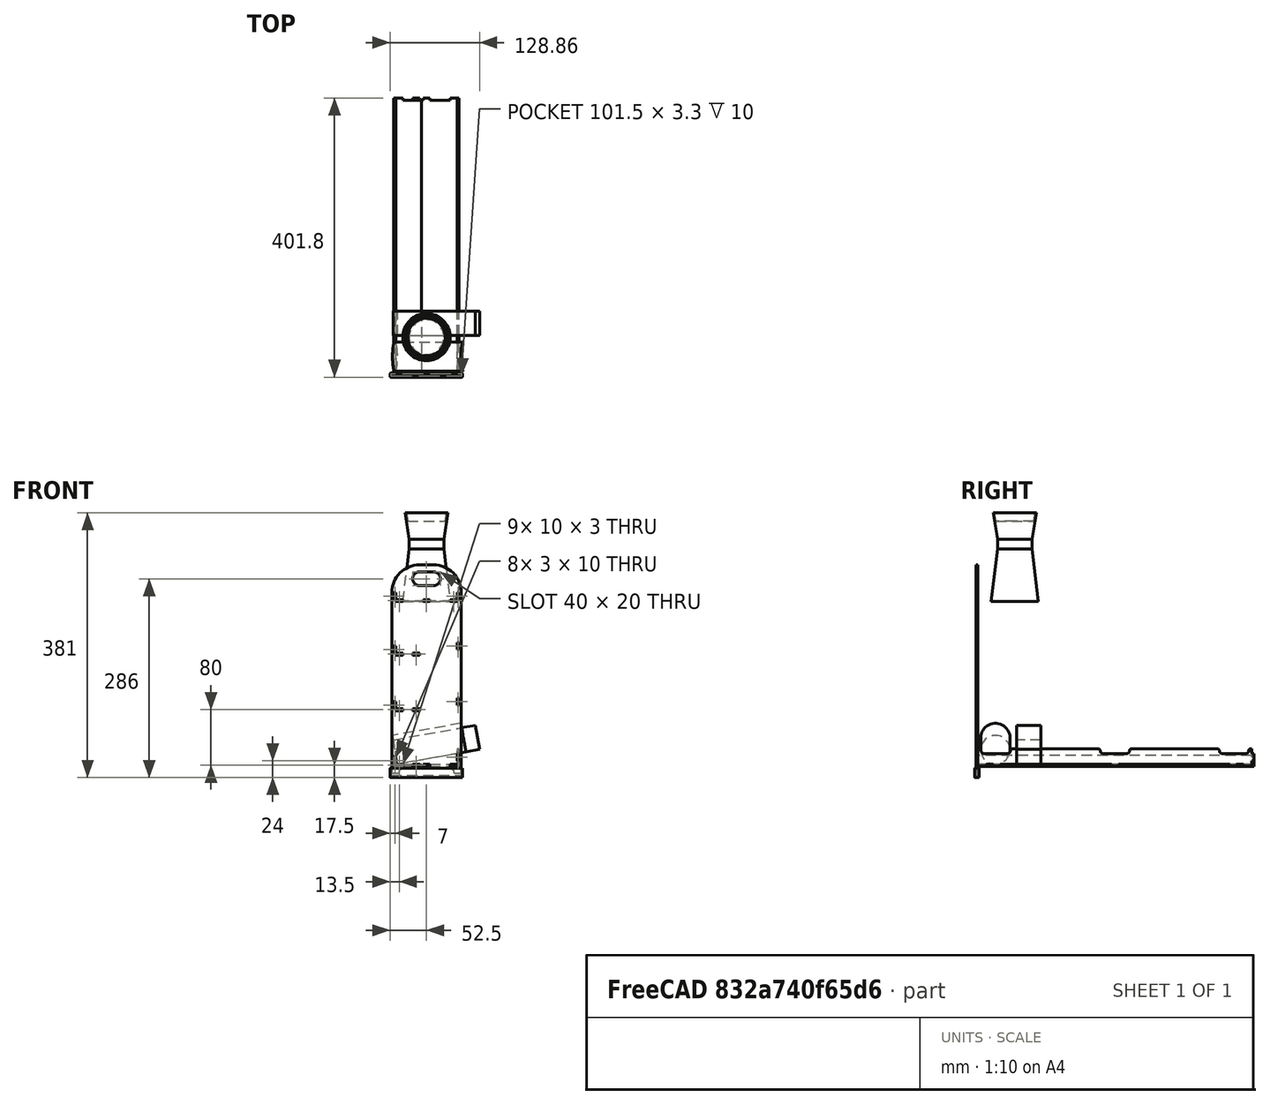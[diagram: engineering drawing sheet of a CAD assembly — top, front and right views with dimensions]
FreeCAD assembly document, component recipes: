
FREECAD ASSEMBLY — COMPONENT RECIPES ("stockage_epices")

This assembly document has 12 components, labeled P0..P11 below (a component is one placed body or linked part). 12 of them carry a construction recipe — the FreeCAD feature program that regenerates the part from scratch, quoted from this document or its linked companion documents; the rest are supplied as boundary geometry only. No exploded tour is included for this assembly.
COMPONENT P0 — recipe-attached ("BackR003", modeled in this document).
Construction recipe (the document's own serialized feature program — sketch geometry with constraints, then the solid features built on it; lengths are millimeters unless a unit is written):

FEATURE [Sketcher::SketchObject] Sketch004
  ArcFitTolerance = 0
  FullyConstrained = true
  MakeInternals = false
  MapMode = 5
  Placement = pos=(0,0,0) rot=(0.57735,0.57735,0.57735;2.0944rad)
  sketch-geometry (12):
    g0: LineSegment StartX=394 StartY=0 StartZ=0 EndX=0 EndY=0 EndZ=0
    g1: LineSegment StartX=394 StartY=-13 StartZ=0 EndX=397 EndY=-13 EndZ=0
    g2: LineSegment StartX=397 StartY=-13 StartZ=0 EndX=397 EndY=-3 EndZ=0
    g3: LineSegment StartX=397 StartY=-3 StartZ=0 EndX=394 EndY=-3 EndZ=0
    g4: LineSegment StartX=0 StartY=-3 StartZ=0 EndX=-3 EndY=-3 EndZ=0
    g5: LineSegment StartX=-3 StartY=-3 StartZ=0 EndX=-3 EndY=-13 EndZ=0
    g6: LineSegment StartX=-3 StartY=-13 StartZ=0 EndX=0 EndY=-13 EndZ=0
    g7: LineSegment StartX=0 StartY=-3 StartZ=0 EndX=0 EndY=0 EndZ=0
    g8: LineSegment StartX=0 StartY=-13 StartZ=0 EndX=0 EndY=-16 EndZ=0
    g9: LineSegment StartX=394 StartY=-3 StartZ=0 EndX=394 EndY=0 EndZ=0
    g10: LineSegment StartX=394 StartY=-13 StartZ=0 EndX=394 EndY=-16 EndZ=0
    g11: LineSegment StartX=0 StartY=-16 StartZ=0 EndX=394 EndY=-16 EndZ=0
  constraints (36):
    c: Horizontal(g0)
    c: Distance(g0,g0) = 394
    c: Coincident(g1,g2)
    c: Coincident(g2,g3)
    c: Horizontal(g1)
    c: Horizontal(g3)
    c: Vertical(g2)
    c: Distance(g2,g1) = 3
    c: Coincident(g4,g5)
    c: Coincident(g5,g6)
    c: Horizontal(g4)
    c: Horizontal(g6)
    c: Vertical(g5)
    c: Distance(g5,g4) = 3
    c: Equal(g5,g2)
    c: Horizontal(g1,g5)
    c: DistanceY(g5,g5) = 10
    c: DistanceY(g4,g0) = 3
    c: Coincident(g7,g4)
    c: Coincident(g7,g0)
    c: Vertical(g7)
    c: Coincident(g8,g6)
    c: PointOnObject(g8,g-2)
    c: Vertical(g8)
    c: Coincident(g9,g3)
    c: Coincident(g9,g0)
    c: Vertical(g9)
    c: Coincident(g10,g1)
    c: Vertical(g10)
    c: Equal(g1,g3)
    c: PointOnObject(g0,g-1)
    c: PointOnObject(g4,g-2)
    c: Equal(g7,g8)
    c: Equal(g9,g10)
    c: Coincident(g11,g8)
    c: Coincident(g11,g10)
FEATURE [PartDesign::Pad] Pad003
  Direction = (1,1e-16,-1e-16)
  Length = 3
  Length2 = 10
  Placement = pos=(0,0,0) rot=(0.57735,0.57735,0.57735;2.0944rad)
  Profile = -> Sketch004
  Refine = true
  Suppressed = false
  Type = 0
FEATURE [Sketcher::SketchObject] Sketch005
  ArcFitTolerance = 0
  ExternalGeometry = -> [Pad003]
  FullyConstrained = true
  MakeInternals = false
  MapMode = 5
  Placement = pos=(3,-1e-15,0) rot=(0.57735,0.57735,0.57735;2.0944rad)
  sketch-geometry (4):
    g0: LineSegment StartX=12 StartY=-16 StartZ=0 EndX=22 EndY=-16 EndZ=0
    g1: LineSegment StartX=22 StartY=-16 StartZ=0 EndX=22 EndY=-13 EndZ=0
    g2: LineSegment StartX=22 StartY=-13 StartZ=0 EndX=12 EndY=-13 EndZ=0
    g3: LineSegment StartX=12 StartY=-13 StartZ=0 EndX=12 EndY=-16 EndZ=0
  constraints (12):
    c: Coincident(g0,g1)
    c: Coincident(g1,g2)
    c: Coincident(g2,g3)
    c: Coincident(g3,g0)
    c: Horizontal(g0)
    c: Horizontal(g2)
    c: Vertical(g1)
    c: Vertical(g3)
    c: Distance(g1,g3) = 10
    c: Distance(g0,g2) = 3
    c: PointOnObject(g0,g-3)
    c: DistanceX(g-1,g2) = 12
FEATURE [PartDesign::Pocket] Pocket001
  BaseFeature = -> Pad003
  Direction = (-1,-1e-16,1e-16)
  Length = 5
  Length2 = 5
  Placement = pos=(0,0,0) rot=(0.57735,0.57735,0.57735;2.0944rad)
  Profile = -> Sketch005
  Refine = true
  Suppressed = false
  Type = 2
FEATURE [PartDesign::LinearPattern] LinearPattern001
  BaseFeature = -> Pocket001
  Direction = -> Sketch005 [H_Axis]
  Length = 360
  Mode = 0
  Occurrences = 3
  Offset = 180
  Originals = -> [Pocket001]
  Placement = pos=(0,0,0) rot=(0.57735,0.57735,0.57735;2.0944rad)
  Refine = true
  Suppressed = false
  TransformMode = 0
FEATURE [PartDesign::Body] Body003  label="BackR1"
  AllowCompound = false
  Group = -> [Sketch004,Pad003,Sketch005,Pocket001,LinearPattern001]
  Origin = -> Origin003
  Placement = pos=(0,0,29) rot=(0,0,1;0rad)
  Tip = -> LinearPattern001
COMPONENT P1 — same part as P0; its construction recipe is shown at P0.
COMPONENT P2 — recipe-attached ("Epice_rond", modeled in this document).
Construction recipe (the document's own serialized feature program — sketch geometry with constraints, then the solid features built on it; lengths are millimeters unless a unit is written):

FEATURE [Sketcher::SketchObject] Sketch
  ArcFitTolerance = 0
  FullyConstrained = true
  MakeInternals = false
  MapMode = 5
  Placement = pos=(0,0,0) rot=(0.57735,0.57735,0.57735;2.0944rad)
  sketch-geometry (1):
    g0: Circle CenterX=0 CenterY=0 CenterZ=0 NormalX=0 NormalY=0 NormalZ=1 AngleXU=0 Radius=21
  constraints (2):
    c: Diameter(g0) = 42
    c: Coincident(g0,g-1)
FEATURE [PartDesign::Pad] Pad
  Direction = (1,1e-16,-1e-16)
  Length = 100
  Length2 = 10
  Placement = pos=(0,0,0) rot=(0.57735,0.57735,0.57735;2.0944rad)
  Profile = -> Sketch
  Refine = true
  Suppressed = false
  Type = 0
FEATURE [PartDesign::Body] Body  label="Epice_rond"
  AllowCompound = false
  Group = -> [Sketch,Pad]
  Origin = -> Origin
  Placement = pos=(1.62713,25,36.8423) rot=(0,-1,0;0.174533rad)
  Tip = -> Pad
COMPONENT P3 — recipe-attached ("Epice_carre", modeled in this document).
Construction recipe (the document's own serialized feature program — sketch geometry with constraints, then the solid features built on it; lengths are millimeters unless a unit is written):

FEATURE [Sketcher::SketchObject] Sketch001
  ArcFitTolerance = 0
  FullyConstrained = true
  MakeInternals = false
  MapMode = 5
  Placement = pos=(0,0,0) rot=(0.57735,0.57735,0.57735;2.0944rad)
  sketch-geometry (5):
    g0: LineSegment StartX=-17.5 StartY=-17.5 StartZ=0 EndX=17.5 EndY=-17.5 EndZ=0
    g1: LineSegment StartX=17.5 StartY=-17.5 StartZ=0 EndX=17.5 EndY=17.5 EndZ=0
    g2: LineSegment StartX=17.5 StartY=17.5 StartZ=0 EndX=-17.5 EndY=17.5 EndZ=0
    g3: LineSegment StartX=-17.5 StartY=17.5 StartZ=0 EndX=-17.5 EndY=-17.5 EndZ=0
    g4: GeomPoint [constr] X=0 Y=0 Z=0
  constraints (12):
    c: Coincident(g0,g1)
    c: Coincident(g1,g2)
    c: Coincident(g2,g3)
    c: Coincident(g3,g0)
    c: Horizontal(g0)
    c: Horizontal(g2)
    c: Vertical(g1)
    c: Vertical(g3)
    c: Symmetric(g2,g0,g4)
    c: Distance(g1,g3) = 35
    c: Distance(g0,g2) = 35
    c: Coincident(g4,g-1)
FEATURE [PartDesign::Pad] Pad001
  Direction = (1,1e-16,-1e-16)
  Length = 120
  Length2 = 10
  Placement = pos=(0,0,0) rot=(0.57735,0.57735,0.57735;2.0944rad)
  Profile = -> Sketch001
  Refine = true
  Suppressed = false
  Type = 0
FEATURE [PartDesign::Body] Body001  label="Epice_carre"
  AllowCompound = false
  Group = -> [Sketch001,Pad001]
  Origin = -> Origin001
  Placement = pos=(2.14807,73,33.8878) rot=(0,-1,0;0.174533rad)
  Tip = -> Pad001
COMPONENT P4 — recipe-attached ("GratGrat", modeled in this document).
Construction recipe (the document's own serialized feature program — sketch geometry with constraints, then the solid features built on it; lengths are millimeters unless a unit is written):

FEATURE [Sketcher::SketchObject] Sketch013
  ArcFitTolerance = 0
  FullyConstrained = true
  MakeInternals = false
  MapMode = 5
  Placement = pos=(0,0,0) rot=(1,0,0;1.5708rad)
  sketch-geometry (8):
    g0: LineSegment StartX=0 StartY=0 StartZ=0 EndX=-34 EndY=0 EndZ=0
    g1: LineSegment StartX=-34 StartY=0 StartZ=0 EndX=-25 EndY=76 EndZ=0
    g2: LineSegment StartX=-25 StartY=76 StartZ=0 EndX=-25 EndY=90 EndZ=0
    g3: LineSegment StartX=-25 StartY=90 StartZ=0 EndX=-31 EndY=128 EndZ=0
    g4: LineSegment StartX=-31 StartY=128 StartZ=0 EndX=-29 EndY=128 EndZ=0
    g5: LineSegment StartX=-29 StartY=128 StartZ=0 EndX=-27.1053 EndY=116 EndZ=0
    g6: LineSegment StartX=-27.1053 StartY=116 StartZ=0 EndX=0 EndY=116 EndZ=0
    g7: LineSegment StartX=0 StartY=116 StartZ=0 EndX=0 EndY=0 EndZ=0
  constraints (23):
    c: Coincident(g-1,g0)
    c: Horizontal(g0)
    c: Coincident(g0,g1)
    c: Coincident(g1,g2)
    c: Vertical(g2)
    c: Coincident(g2,g3)
    c: Coincident(g3,g4)
    c: Horizontal(g4)
    c: Coincident(g4,g5)
    c: Coincident(g5,g6)
    c: Horizontal(g6)
    c: Coincident(g6,g7)
    c: Coincident(g7,g0)
    c: Vertical(g7)
    c: DistanceX(g0,g0) = 34
    c: Distance(g7,g2) = 25
    c: Distance(g3,g-2) = 31
    c: Parallel(g5,g3)
    c: DistanceY(g2,g2) = 14
    c: DistanceY(g0,g1) = 76
    c: Distance(g4,g4) = 2
    c: DistanceY(g0,g3) = 128
    c: DistanceY(g6,g4) = 12
FEATURE [PartDesign::Revolution] Revolution
  Angle = 360
  Angle2 = 60
  Axis = (0,0,1)
  Base = (0,0,0)
  Placement = pos=(0,0,0) rot=(1,0,0;1.5708rad)
  Profile = -> Sketch013
  ReferenceAxis = -> Sketch013 [V_Axis]
  Refine = true
  Suppressed = false
  Type = 0
FEATURE [PartDesign::Body] Body007  label="GratGrat"
  AllowCompound = false
  Group = -> [Sketch013,Revolution]
  Origin = -> Origin010
  Placement = pos=(47,53,250) rot=(0,0,1;0rad)
  Tip = -> Revolution
COMPONENT P5 — recipe-attached ("Part001", modeled in this document).
Construction recipe (the document's own serialized feature program — sketch geometry with constraints, then the solid features built on it; lengths are millimeters unless a unit is written):

FEATURE [Sketcher::SketchObject] Sketch015
  ArcFitTolerance = 1e-06
  AttachmentSupport = -> [XY_Plane012]
  FullyConstrained = true
  MakeInternals = false
  MapMode = 5
  sketch-geometry (14):
    g0: LineSegment StartX=-4 StartY=0 StartZ=0 EndX=-4 EndY=-3.3 EndZ=0
    g1: LineSegment StartX=-4 StartY=-3.3 StartZ=0 EndX=97.5 EndY=-3.3 EndZ=0
    g2: LineSegment StartX=97.5 StartY=-3.3 StartZ=0 EndX=97.5 EndY=0 EndZ=0
    g3: LineSegment StartX=97.5 StartY=0 StartZ=0 EndX=-4 EndY=0 EndZ=0
    g4: LineSegment StartX=-5.5 StartY=2e-16 StartZ=0 EndX=-5.5 EndY=-3.3 EndZ=0
    g5: LineSegment StartX=-4 StartY=-4.8 StartZ=0 EndX=97.5 EndY=-4.8 EndZ=0
    g6: LineSegment StartX=99 StartY=-3.3 StartZ=0 EndX=99 EndY=0 EndZ=0
    g7: LineSegment StartX=97.5 StartY=1.5 StartZ=0 EndX=-4 EndY=1.5 EndZ=0
    g8: ArcOfCircle CenterX=-4 CenterY=0 CenterZ=0 NormalX=0 NormalY=0 NormalZ=1 AngleXU=0 Radius=1.5 StartAngle=1.5708 EndAngle=3.14159
    g9: ArcOfCircle CenterX=-4 CenterY=-3.3 CenterZ=0 NormalX=0 NormalY=0 NormalZ=1 AngleXU=0 Radius=1.5 StartAngle=3.14159 EndAngle=4.71239
    g10: ArcOfCircle CenterX=97.5 CenterY=-3.3 CenterZ=0 NormalX=0 NormalY=0 NormalZ=1 AngleXU=0 Radius=1.5 StartAngle=4.71239 EndAngle=6.28319
    g11: ArcOfCircle CenterX=97.5 CenterY=1e-16 CenterZ=0 NormalX=0 NormalY=0 NormalZ=1 AngleXU=0 Radius=1.5 StartAngle=0 EndAngle=1.5708
    g12: GeomPoint [constr] X=-5.5 Y=1.5 Z=0
    g13: GeomPoint [constr] X=99 Y=-4.8 Z=0
  constraints (34):
    c: Coincident(g0,g1)
    c: Coincident(g1,g2)
    c: Coincident(g2,g3)
    c: Coincident(g3,g0)
    c: Vertical(g0)
    c: Vertical(g2)
    c: Horizontal(g1)
    c: Horizontal(g3)
    c: Distance(g0,g2) = 101.5
    c: Distance(g1,g3) = 3.3
    c: PointOnObject(g0,g-1)
    c: Tangent(g4,g8) = -1.5708
    c: Tangent(g4,g9) = -1.5708
    c: Tangent(g5,g9) = -1.5708
    c: Tangent(g5,g10) = -1.5708
    c: Tangent(g6,g10) = -1.5708
    c: Tangent(g6,g11) = -1.5708
    c: Tangent(g7,g11) = -1.5708
    c: Tangent(g7,g8) = -1.5708
    c: Vertical(g4)
    c: Vertical(g6)
    c: Horizontal(g5)
    c: Horizontal(g7)
    c: Equal(g8,g9)
    c: Equal(g9,g10)
    c: Equal(g10,g11)
    c: PointOnObject(g12,g4)
    c: PointOnObject(g12,g7)
    c: PointOnObject(g13,g5)
    c: PointOnObject(g13,g6)
    c: Radius(g9) = 1.5
    c: Coincident(g8,g0)
    c: Coincident(g10,g1)
    c: Distance(g-2,g0) = 4
FEATURE [PartDesign::Pad] Pad007
  Direction = (0,0,1)
  Length = 10
  Length2 = 10
  Profile = -> Sketch015
  ReferenceAxis = -> Sketch015 [N_Axis]
  Suppressed = false
  Type = 0
FEATURE [Sketcher::SketchObject] Sketch016
  ArcFitTolerance = 1e-06
  AttachmentSupport = -> [Pad007]
  ExternalGeometry = -> [Pad007]
  FullyConstrained = true
  MakeInternals = false
  MapMode = 5
  Placement = pos=(0,0,0) rot=(1,0,0;3.14159rad)
  sketch-geometry (10):
    g0: LineSegment StartX=-5.5 StartY=3.3 StartZ=0 EndX=-5.5 EndY=0 EndZ=0
    g1: LineSegment StartX=-4 StartY=-1.5 StartZ=0 EndX=97.5 EndY=-1.5 EndZ=0
    g2: LineSegment StartX=99 StartY=-1e-16 StartZ=0 EndX=99 EndY=3.3 EndZ=0
    g3: LineSegment StartX=97.5 StartY=4.8 StartZ=0 EndX=-4 EndY=4.8 EndZ=0
    g4: ArcOfCircle CenterX=-4 CenterY=3.3 CenterZ=0 NormalX=0 NormalY=0 NormalZ=1 AngleXU=0 Radius=1.5 StartAngle=1.5708 EndAngle=3.14159
    g5: ArcOfCircle CenterX=-4 CenterY=0 CenterZ=0 NormalX=0 NormalY=0 NormalZ=1 AngleXU=0 Radius=1.5 StartAngle=3.14159 EndAngle=4.71239
    g6: ArcOfCircle CenterX=97.5 CenterY=-1e-16 CenterZ=0 NormalX=0 NormalY=0 NormalZ=1 AngleXU=0 Radius=1.5 StartAngle=4.71239 EndAngle=6.28319
    g7: ArcOfCircle CenterX=97.5 CenterY=3.3 CenterZ=0 NormalX=0 NormalY=0 NormalZ=1 AngleXU=0 Radius=1.5 StartAngle=0 EndAngle=1.5708
    g8: GeomPoint [constr] X=-5.5 Y=4.8 Z=0
    g9: GeomPoint [constr] X=99 Y=-1.5 Z=0
  constraints (21):
    c: Tangent(g0,g4) = -1.5708
    c: Tangent(g0,g5) = -1.5708
    c: Tangent(g1,g5) = -1.5708
    c: Tangent(g1,g6) = -1.5708
    c: Tangent(g2,g6) = -1.5708
    c: Tangent(g2,g7) = -1.5708
    c: Tangent(g3,g7) = -1.5708
    c: Tangent(g3,g4) = -1.5708
    c: Vertical(g2)
    c: Horizontal(g1)
    c: Horizontal(g3)
    c: Equal(g4,g5)
    c: Equal(g5,g6)
    c: Equal(g6,g7)
    c: PointOnObject(g8,g0)
    c: PointOnObject(g8,g3)
    c: PointOnObject(g9,g1)
    c: PointOnObject(g9,g2)
    c: Coincident(g6,g-4)
    c: Coincident(g4,g-3)
    c: Coincident(g0,g-3)
FEATURE [PartDesign::Pad] Pad008
  BaseFeature = -> Pad007
  Direction = (0,0,-1)
  Length = 3
  Length2 = 10
  Profile = -> Sketch016
  ReferenceAxis = -> Sketch016 [N_Axis]
  Suppressed = false
  Type = 0
FEATURE [PartDesign::Body] Body008  label="Body"
  AllowCompound = false
  Group = -> [Sketch015,Pad007,Sketch016,Pad008]
  Origin = -> Origin012
  Tip = -> Pad008
COMPONENT P6 — recipe-attached ("RackBot", modeled in this document).
Construction recipe (the document's own serialized feature program — sketch geometry with constraints, then the solid features built on it; lengths are millimeters unless a unit is written):

FEATURE [Sketcher::SketchObject] Sketch002
  ArcFitTolerance = 0
  FullyConstrained = true
  MakeInternals = false
  MapMode = 5
  Placement = pos=(0,0,0) rot=(0.57735,0.57735,0.57735;2.0944rad)
  sketch-geometry (12):
    g0: LineSegment StartX=0 StartY=-17.5 StartZ=0 EndX=394 EndY=-17.5 EndZ=0
    g1: LineSegment StartX=0 StartY=-17.5 StartZ=0 EndX=0 EndY=-10 EndZ=0
    g2: LineSegment StartX=0 StartY=-10 StartZ=0 EndX=-3 EndY=-10 EndZ=0
    g3: LineSegment StartX=-3 StartY=-10 StartZ=0 EndX=-3 EndY=0 EndZ=0
    g4: LineSegment StartX=-3 StartY=0 StartZ=0 EndX=0 EndY=0 EndZ=0
    g5: LineSegment StartX=0 StartY=0 StartZ=0 EndX=0 EndY=7.5 EndZ=0
    g6: LineSegment StartX=0 StartY=7.5 StartZ=0 EndX=394 EndY=7.5 EndZ=0
    g7: LineSegment StartX=394 StartY=7.5 StartZ=0 EndX=394 EndY=0 EndZ=0
    g8: LineSegment StartX=394 StartY=0 StartZ=0 EndX=397 EndY=0 EndZ=0
    g9: LineSegment StartX=397 StartY=0 StartZ=0 EndX=397 EndY=-10 EndZ=0
    g10: LineSegment StartX=397 StartY=-10 StartZ=0 EndX=394 EndY=-10 EndZ=0
    g11: LineSegment StartX=394 StartY=-10 StartZ=0 EndX=394 EndY=-17.5 EndZ=0
  constraints (35):
    c: PointOnObject(g0,g-2)
    c: Horizontal(g0)
    c: Coincident(g0,g1)
    c: PointOnObject(g1,g-2)
    c: Coincident(g1,g2)
    c: Coincident(g2,g3)
    c: PointOnObject(g3,g-1)
    c: Vertical(g3)
    c: Coincident(g3,g4)
    c: Coincident(g4,g-1)
    c: Coincident(g4,g5)
    c: PointOnObject(g5,g-2)
    c: Horizontal(g2)
    c: Distance(g2,g2) = 3
    c: Coincident(g6,g5)
    c: Horizontal(g6)
    c: Coincident(g7,g6)
    c: PointOnObject(g7,g-1)
    c: Vertical(g7)
    c: Coincident(g8,g7)
    c: PointOnObject(g8,g-1)
    c: Coincident(g9,g8)
    c: Vertical(g9)
    c: Horizontal(g10)
    c: Vertical(g11)
    c: Coincident(g0,g11)
    c: Coincident(g10,g11)
    c: Equal(g1,g11)
    c: Equal(g2,g10)
    c: Coincident(g10,g9)
    c: Vertical(g10,g7)
    c: Equal(g5,g1)
    c: DistanceX(g3,g8) = 400
    c: DistanceY(g0,g6) = 25
    c: DistanceY(g3,g3) = 10
FEATURE [PartDesign::Pad] Pad002
  Direction = (1,1e-16,-1e-16)
  Length = 3
  Length2 = 10
  Placement = pos=(0,0,0) rot=(0.57735,0.57735,0.57735;2.0944rad)
  Profile = -> Sketch002
  Refine = true
  Suppressed = false
  Type = 0
FEATURE [Sketcher::SketchObject] Sketch003
  ArcFitTolerance = 0
  ExternalGeometry = -> [Pad002]
  FullyConstrained = true
  MakeInternals = false
  MapMode = 5
  Placement = pos=(3,-1e-15,0) rot=(0.57735,0.57735,0.57735;2.0944rad)
  sketch-geometry (6):
    g0: ArcOfCircle CenterX=8 CenterY=4 CenterZ=0 NormalX=0 NormalY=0 NormalZ=1 AngleXU=0 Radius=3.5 StartAngle=3.14159 EndAngle=4.71239
    g1: ArcOfCircle CenterX=50 CenterY=4 CenterZ=0 NormalX=0 NormalY=0 NormalZ=1 AngleXU=0 Radius=3.5 StartAngle=1.5708 EndAngle=3.14159
    g2: ArcOfCircle CenterX=43 CenterY=4 CenterZ=0 NormalX=0 NormalY=0 NormalZ=1 AngleXU=0 Radius=3.5 StartAngle=4.71239 EndAngle=6.28319
    g3: LineSegment StartX=8 StartY=0.500003 StartZ=0 EndX=43 EndY=0.500003 EndZ=0
    g4: LineSegment StartX=1 StartY=7.5 StartZ=0 EndX=50 EndY=7.5 EndZ=0
    g5: ArcOfCircle CenterX=1 CenterY=4 CenterZ=0 NormalX=0 NormalY=0 NormalZ=1 AngleXU=0 Radius=3.5 StartAngle=0 EndAngle=1.5708
  constraints (23):
    c: Coincident(g2,g1)
    c: Coincident(g3,g0)
    c: Coincident(g3,g2)
    c: Equal(g0,g2)
    c: Horizontal(g3)
    c: Vertical(g0,g0)
    c: Vertical(g1,g1)
    c: Coincident(g4,g1)
    c: DistanceX(g0,g1) = 42
    c: DistanceX(g3,g3) = 35
    c: Coincident(g5,g0)
    c: Coincident(g5,g4)
    c: PointOnObject(g4,g-3)
    c: Vertical(g4,g5)
    c: Horizontal(g4)
    c: DistanceX(g-3,g4) = 1
    c: DistanceX(g4,g1) = 49
    c: Horizontal(g1,g0)
    c: Horizontal(g0,g2)
    c: Horizontal(g2,g0)
    c: Horizontal(g2,g5)
    c: Horizontal(g5,g1)
    c: Equal(g5,g0)
FEATURE [PartDesign::Pocket] Pocket
  BaseFeature = -> Pad002
  Direction = (-1,-1e-16,1e-16)
  Length = 0
  Length2 = 5
  Placement = pos=(0,0,0) rot=(0.57735,0.57735,0.57735;2.0944rad)
  Profile = -> Sketch003
  Refine = true
  Suppressed = false
  Type = 2
FEATURE [PartDesign::LinearPattern] LinearPattern
  BaseFeature = -> Pocket
  Direction = -> Sketch003 [H_Axis]
  Length = 343
  Mode = 0
  Occurrences = 3
  Offset = 171.5
  Originals = -> [Pocket]
  Placement = pos=(0,0,0) rot=(0.57735,0.57735,0.57735;2.0944rad)
  Refine = true
  Suppressed = false
  TransformMode = 0
FEATURE [PartDesign::Body] Body002  label="Front_r1"
  AllowCompound = false
  Group = -> [Sketch002,Pad002,Sketch003,Pocket,LinearPattern]
  Origin = -> Origin002
  Placement = pos=(91,0,31) rot=(0,0,1;0rad)
  Tip = -> LinearPattern
FEATURE [Sketcher::SketchObject] Sketch004
  ArcFitTolerance = 0
  FullyConstrained = true
  MakeInternals = false
  MapMode = 5
  Placement = pos=(0,0,0) rot=(0.57735,0.57735,0.57735;2.0944rad)
  sketch-geometry (12):
    g0: LineSegment StartX=394 StartY=0 StartZ=0 EndX=0 EndY=0 EndZ=0
    g1: LineSegment StartX=394 StartY=-13 StartZ=0 EndX=397 EndY=-13 EndZ=0
    g2: LineSegment StartX=397 StartY=-13 StartZ=0 EndX=397 EndY=-3 EndZ=0
    g3: LineSegment StartX=397 StartY=-3 StartZ=0 EndX=394 EndY=-3 EndZ=0
    g4: LineSegment StartX=0 StartY=-3 StartZ=0 EndX=-3 EndY=-3 EndZ=0
    g5: LineSegment StartX=-3 StartY=-3 StartZ=0 EndX=-3 EndY=-13 EndZ=0
    g6: LineSegment StartX=-3 StartY=-13 StartZ=0 EndX=0 EndY=-13 EndZ=0
    g7: LineSegment StartX=0 StartY=-3 StartZ=0 EndX=0 EndY=0 EndZ=0
    g8: LineSegment StartX=0 StartY=-13 StartZ=0 EndX=0 EndY=-16 EndZ=0
    g9: LineSegment StartX=394 StartY=-3 StartZ=0 EndX=394 EndY=0 EndZ=0
    g10: LineSegment StartX=394 StartY=-13 StartZ=0 EndX=394 EndY=-16 EndZ=0
    g11: LineSegment StartX=0 StartY=-16 StartZ=0 EndX=394 EndY=-16 EndZ=0
  constraints (36):
    c: Horizontal(g0)
    c: Distance(g0,g0) = 394
    c: Coincident(g1,g2)
    c: Coincident(g2,g3)
    c: Horizontal(g1)
    c: Horizontal(g3)
    c: Vertical(g2)
    c: Distance(g2,g1) = 3
    c: Coincident(g4,g5)
    c: Coincident(g5,g6)
    c: Horizontal(g4)
    c: Horizontal(g6)
    c: Vertical(g5)
    c: Distance(g5,g4) = 3
    c: Equal(g5,g2)
    c: Horizontal(g1,g5)
    c: DistanceY(g5,g5) = 10
    c: DistanceY(g4,g0) = 3
    c: Coincident(g7,g4)
    c: Coincident(g7,g0)
    c: Vertical(g7)
    c: Coincident(g8,g6)
    c: PointOnObject(g8,g-2)
    c: Vertical(g8)
    c: Coincident(g9,g3)
    c: Coincident(g9,g0)
    c: Vertical(g9)
    c: Coincident(g10,g1)
    c: Vertical(g10)
    c: Equal(g1,g3)
    c: PointOnObject(g0,g-1)
    c: PointOnObject(g4,g-2)
    c: Equal(g7,g8)
    c: Equal(g9,g10)
    c: Coincident(g11,g8)
    c: Coincident(g11,g10)
FEATURE [PartDesign::Pad] Pad003
  Direction = (1,1e-16,-1e-16)
  Length = 3
  Length2 = 10
  Placement = pos=(0,0,0) rot=(0.57735,0.57735,0.57735;2.0944rad)
  Profile = -> Sketch004
  Refine = true
  Suppressed = false
  Type = 0
FEATURE [Sketcher::SketchObject] Sketch005
  ArcFitTolerance = 0
  ExternalGeometry = -> [Pad003]
  FullyConstrained = true
  MakeInternals = false
  MapMode = 5
  Placement = pos=(3,-1e-15,0) rot=(0.57735,0.57735,0.57735;2.0944rad)
  sketch-geometry (4):
    g0: LineSegment StartX=12 StartY=-16 StartZ=0 EndX=22 EndY=-16 EndZ=0
    g1: LineSegment StartX=22 StartY=-16 StartZ=0 EndX=22 EndY=-13 EndZ=0
    g2: LineSegment StartX=22 StartY=-13 StartZ=0 EndX=12 EndY=-13 EndZ=0
    g3: LineSegment StartX=12 StartY=-13 StartZ=0 EndX=12 EndY=-16 EndZ=0
  constraints (12):
    c: Coincident(g0,g1)
    c: Coincident(g1,g2)
    c: Coincident(g2,g3)
    c: Coincident(g3,g0)
    c: Horizontal(g0)
    c: Horizontal(g2)
    c: Vertical(g1)
    c: Vertical(g3)
    c: Distance(g1,g3) = 10
    c: Distance(g0,g2) = 3
    c: PointOnObject(g0,g-3)
    c: DistanceX(g-1,g2) = 12
FEATURE [PartDesign::Pocket] Pocket001
  BaseFeature = -> Pad003
  Direction = (-1,-1e-16,1e-16)
  Length = 5
  Length2 = 5
  Placement = pos=(0,0,0) rot=(0.57735,0.57735,0.57735;2.0944rad)
  Profile = -> Sketch005
  Refine = true
  Suppressed = false
  Type = 2
FEATURE [PartDesign::LinearPattern] LinearPattern001
  BaseFeature = -> Pocket001
  Direction = -> Sketch005 [H_Axis]
  Length = 360
  Mode = 0
  Occurrences = 3
  Offset = 180
  Originals = -> [Pocket001]
  Placement = pos=(0,0,0) rot=(0.57735,0.57735,0.57735;2.0944rad)
  Refine = true
  Suppressed = false
  TransformMode = 0
FEATURE [PartDesign::Body] Body003  label="BackR1"
  AllowCompound = false
  Group = -> [Sketch004,Pad003,Sketch005,Pocket001,LinearPattern001]
  Origin = -> Origin003
  Placement = pos=(0,0,29) rot=(0,0,1;0rad)
  Tip = -> LinearPattern001
FEATURE [Sketcher::SketchObject] Sketch006
  ArcFitTolerance = 0
  FullyConstrained = true
  MakeInternals = false
  MapMode = 5
  sketch-geometry (21):
    g0: LineSegment StartX=40 StartY=0 StartZ=0 EndX=37 EndY=0 EndZ=0
    g1: LineSegment StartX=37 StartY=0 StartZ=0 EndX=37 EndY=-3 EndZ=0
    g2: LineSegment StartX=3 StartY=-3 StartZ=0 EndX=3 EndY=0 EndZ=0
    g3: LineSegment StartX=0 StartY=12 StartZ=0 EndX=0 EndY=382 EndZ=0
    g4: LineSegment StartX=0 StartY=382 StartZ=0 EndX=3 EndY=382 EndZ=0
    g5: LineSegment StartX=3 StartY=382 StartZ=0 EndX=3 EndY=397 EndZ=0
    g6: LineSegment StartX=37 StartY=397 StartZ=0 EndX=37 EndY=394 EndZ=0
    g7: LineSegment StartX=37 StartY=394 StartZ=0 EndX=40 EndY=394 EndZ=0
    g8: LineSegment StartX=40 StartY=394 StartZ=0 EndX=40 EndY=0 EndZ=0
    g9: LineSegment StartX=13 StartY=-3 StartZ=0 EndX=13 EndY=0 EndZ=0
    g10: LineSegment StartX=13 StartY=0 StartZ=0 EndX=27 EndY=0 EndZ=0
    g11: LineSegment StartX=27 StartY=0 StartZ=0 EndX=27 EndY=-3 EndZ=0
    g12: LineSegment StartX=3 StartY=397 StartZ=0 EndX=13 EndY=397 EndZ=0
    g13: LineSegment StartX=13 StartY=397 StartZ=0 EndX=13 EndY=394 EndZ=0
    g14: LineSegment StartX=13 StartY=394 StartZ=0 EndX=27 EndY=394 EndZ=0
    g15: LineSegment StartX=27 StartY=394 StartZ=0 EndX=27 EndY=397 EndZ=0
    g16: LineSegment StartX=27 StartY=397 StartZ=0 EndX=37 EndY=397 EndZ=0
    g17: LineSegment StartX=3 StartY=-3 StartZ=0 EndX=13 EndY=-3 EndZ=0
    g18: LineSegment StartX=27 StartY=-3 StartZ=0 EndX=37 EndY=-3 EndZ=0
    g19: LineSegment StartX=0 StartY=12 StartZ=0 EndX=3 EndY=12 EndZ=0
    g20: LineSegment StartX=3 StartY=0 StartZ=0 EndX=3 EndY=12 EndZ=0
  constraints (63):
    c: PointOnObject(g0,g-1)
    c: Horizontal(g0)
    c: Coincident(g0,g1)
    c: Vertical(g1)
    c: Vertical(g2)
    c: PointOnObject(g3,g-2)
    c: Coincident(g3,g4)
    c: Horizontal(g4)
    c: Coincident(g4,g5)
    c: Vertical(g5)
    c: Vertical(g6)
    c: Coincident(g6,g7)
    c: Horizontal(g7)
    c: Coincident(g7,g8)
    c: Coincident(g8,g0)
    c: Vertical(g8)
    c: Distance(g1,g1) = 3
    c: Distance(g5,g2) = 400
    c: DistanceX(g-1,g2) = 3
    c: Distance(g7,g-2) = 40
    c: PointOnObject(g9,g-1)
    c: Vertical(g9)
    c: Coincident(g9,g10)
    c: PointOnObject(g10,g-1)
    c: Coincident(g10,g11)
    c: Vertical(g11)
    c: Coincident(g5,g12)
    c: Horizontal(g12)
    c: Coincident(g12,g13)
    c: Vertical(g13)
    c: Coincident(g13,g14)
    c: Horizontal(g14)
    c: Coincident(g14,g15)
    c: Vertical(g15)
    c: Coincident(g15,g16)
    c: Coincident(g16,g6)
    c: Horizontal(g16)
    c: Horizontal(g14,g6)
    c: Coincident(g17,g2)
    c: Coincident(g17,g9)
    c: Horizontal(g17)
    c: Coincident(g18,g11)
    c: Coincident(g18,g1)
    c: Horizontal(g18)
    c: Equal(g18,g17)
    c: Equal(g17,g12)
    c: Equal(g12,g16)
    c: DistanceX(g12,g12) = 10
    c: Horizontal(g15,g12)
    c: Horizontal(g9,g11)
    c: DistanceY(g5,g5) = 15
    c: Equal(g4,g7)
    c: Equal(g6,g1)
    c: Coincident(g20,g2)
    c: Coincident(g20,g19)
    c: Vertical(g20)
    c: Horizontal(g19)
    c: Coincident(g3,g19)
    c: Vertical(g3)
    c: Equal(g19,g0)
    c: PointOnObject(g2,g-1)
    c: DistanceY(g20,g20) = 12
    c: Equal(g7,g0)
FEATURE [PartDesign::Pad] Pad004
  Direction = (0,0,1)
  Length = 3
  Length2 = 10
  Profile = -> Sketch006
  Refine = true
  Suppressed = false
  Type = 0
FEATURE [Sketcher::SketchObject] Sketch007
  ArcFitTolerance = 0
  ExternalGeometry = -> [Pad004]
  FullyConstrained = true
  MakeInternals = false
  MapMode = 5
  Placement = pos=(0,0,0) rot=(1,0,0;3.14159rad)
  sketch-geometry (4):
    g0: LineSegment StartX=0 StartY=-32 StartZ=0 EndX=3 EndY=-32 EndZ=0
    g1: LineSegment StartX=3 StartY=-32 StartZ=0 EndX=3 EndY=-22 EndZ=0
    g2: LineSegment StartX=3 StartY=-22 StartZ=0 EndX=0 EndY=-22 EndZ=0
    g3: LineSegment StartX=0 StartY=-22 StartZ=0 EndX=0 EndY=-32 EndZ=0
  constraints (12):
    c: Coincident(g0,g1)
    c: Coincident(g1,g2)
    c: Coincident(g2,g3)
    c: Coincident(g3,g0)
    c: Horizontal(g0)
    c: Horizontal(g2)
    c: Vertical(g1)
    c: Vertical(g3)
    c: Distance(g1,g3) = 3
    c: Distance(g0,g2) = 10
    c: PointOnObject(g0,g-2)
    c: DistanceY(g2,g-3) = 10
FEATURE [PartDesign::Pocket] Pocket002
  BaseFeature = -> Pad004
  Direction = (0,1e-16,1)
  Length = 5
  Length2 = 5
  Profile = -> Sketch007
  Refine = true
  Suppressed = false
  Type = 2
FEATURE [PartDesign::LinearPattern] LinearPattern002
  BaseFeature = -> Pocket002
  Direction = -> Sketch007 [V_Axis]
  Length = 340
  Mode = 0
  Occurrences = 3
  Offset = 170
  Originals = -> [Pocket002]
  Refine = true
  Reversed = true
  Suppressed = false
  TransformMode = 0
FEATURE [PartDesign::Body] Body004  label="BotR1"
  AllowCompound = false
  Group = -> [Sketch006,Pad004,Sketch007,Pocket002,LinearPattern002]
  Origin = -> Origin004
  Placement = pos=(0,0,13) rot=(0,0,1;0rad)
  Tip = -> LinearPattern002
COMPONENT P7 — same part as P6; its construction recipe is shown at P6.
COMPONENT P8 — same part as P6; its construction recipe is shown at P6.
COMPONENT P9 — recipe-attached ("SideLeft", modeled in this document).
Construction recipe (the document's own serialized feature program — sketch geometry with constraints, then the solid features built on it; lengths are millimeters unless a unit is written):

FEATURE [Sketcher::SketchObject] Sketch008
  ArcFitTolerance = 0
  FullyConstrained = true
  MakeInternals = false
  MapMode = 5
  Placement = pos=(0,0,0) rot=(1,0,0;1.5708rad)
  sketch-geometry (16):
    g0: LineSegment StartX=-3 StartY=260 StartZ=0 EndX=-3 EndY=0 EndZ=0
    g1: LineSegment StartX=-3 StartY=9e-16 StartZ=0 EndX=7 EndY=9e-16 EndZ=0
    g2: LineSegment StartX=97 StartY=0 StartZ=0 EndX=97 EndY=260 EndZ=0
    g3: LineSegment StartX=57 StartY=300 StartZ=0 EndX=37 EndY=300 EndZ=0
    g4: ArcOfCircle CenterX=14 CenterY=0 CenterZ=0 NormalX=0 NormalY=0 NormalZ=1 AngleXU=0 Radius=7 StartAngle=1.5708 EndAngle=3.14159
    g5: ArcOfCircle CenterX=80 CenterY=0 CenterZ=0 NormalX=0 NormalY=0 NormalZ=1 AngleXU=0 Radius=7 StartAngle=0 EndAngle=1.5708
    g6: LineSegment StartX=14 StartY=7 StartZ=0 EndX=80 EndY=7 EndZ=0
    g7: LineSegment StartX=87 StartY=0 StartZ=0 EndX=97 EndY=0 EndZ=0
    g8: ArcOfCircle CenterX=37 CenterY=260 CenterZ=0 NormalX=0 NormalY=0 NormalZ=1 AngleXU=0 Radius=40 StartAngle=1.5708 EndAngle=3.14159
    g9: GeomPoint [constr] X=-3 Y=300 Z=0
    g10: ArcOfCircle CenterX=57 CenterY=260 CenterZ=0 NormalX=0 NormalY=0 NormalZ=1 AngleXU=0 Radius=40 StartAngle=0 EndAngle=1.5708
    g11: GeomPoint [constr] X=97 Y=300 Z=0
    g12: ArcOfCircle CenterX=37 CenterY=280 CenterZ=0 NormalX=0 NormalY=0 NormalZ=1 AngleXU=0 Radius=10 StartAngle=1.5708 EndAngle=4.71239
    g13: ArcOfCircle CenterX=57 CenterY=280 CenterZ=0 NormalX=0 NormalY=0 NormalZ=1 AngleXU=0 Radius=10 StartAngle=4.71239 EndAngle=7.85398
    g14: LineSegment StartX=37 StartY=290 StartZ=0 EndX=57 EndY=290 EndZ=0
    g15: LineSegment StartX=37 StartY=270 StartZ=0 EndX=57 EndY=270 EndZ=0
  constraints (45):
    c: Coincident(g0,g1)
    c: Coincident(g7,g2)
    c: Vertical(g0)
    c: Vertical(g2)
    c: Horizontal(g1)
    c: Horizontal(g3)
    c: Distance(g1,g9) = 300
    c: DistanceX(g9,g11) = 100
    c: Distance(g-1,g0) = 3
    c: PointOnObject(g4,g1)
    c: PointOnObject(g5,g1)
    c: PointOnObject(g5,g7)
    c: Coincident(g6,g4)
    c: Coincident(g6,g5)
    c: Horizontal(g6)
    c: Vertical(g5,g5)
    c: Vertical(g4,g4)
    c: Coincident(g1,g4)
    c: PointOnObject(g7,g5)
    c: Equal(g1,g7)
    c: DistanceX(g1,g1) = 10
    c: Distance(g4,g4) = 7
    c: Horizontal(g7)
    c: Horizontal(g5,g5)
    c: PointOnObject(g-1,g1)
    c: PointOnObject(g9,g0)
    c: PointOnObject(g9,g3)
    c: Tangent(g0,g8) = -1.5708
    c: Tangent(g3,g8) = -1.5708
    c: PointOnObject(g11,g2)
    c: PointOnObject(g11,g3)
    c: Tangent(g2,g10) = -1.5708
    c: Tangent(g3,g10) = -1.5708
    c: Equal(g8,g10)
    c: Radius(g8) = 40
    c: Tangent(g12,g14) = 1.5708
    c: Tangent(g12,g15) = -1.5708
    c: Tangent(g13,g14) = 1.5708
    c: Tangent(g13,g15) = -1.5708
    c: Equal(g12,g13)
    c: Horizontal(g15)
    c: Radius(g12) = 10
    c: Vertical(g8,g12)
    c: Vertical(g13,g10)
    c: Distance(g3,g12) = 10
FEATURE [PartDesign::Pad] Pad005
  Direction = (0,-1,0)
  Length = 3
  Length2 = 10
  Placement = pos=(0,0,0) rot=(1,0,0;1.5708rad)
  Profile = -> Sketch008
  Refine = true
  Suppressed = false
  Type = 0
FEATURE [Sketcher::SketchObject] Sketch009
  ArcFitTolerance = 0
  ExternalGeometry = -> [Pad005]
  FullyConstrained = true
  MakeInternals = false
  MapMode = 5
  Placement = pos=(0,-3,0) rot=(1,0,0;1.5708rad)
  sketch-geometry (17):
    g0: LineSegment StartX=3 StartY=13 StartZ=0 EndX=3 EndY=23 EndZ=0
    g1: LineSegment StartX=3 StartY=23 StartZ=0 EndX=-1.3e-15 EndY=23 EndZ=0
    g2: LineSegment StartX=-1.3e-15 StartY=23 StartZ=0 EndX=-1.3e-15 EndY=13 EndZ=0
    g3: LineSegment StartX=-1.3e-15 StartY=13 StartZ=0 EndX=3 EndY=13 EndZ=0
    g4: LineSegment StartX=3 StartY=13 StartZ=0 EndX=3 EndY=10 EndZ=0
    g5: LineSegment StartX=3 StartY=10 StartZ=0 EndX=13 EndY=10 EndZ=0
    g6: LineSegment StartX=13 StartY=10 StartZ=0 EndX=13 EndY=13 EndZ=0
    g7: LineSegment StartX=13 StartY=13 StartZ=0 EndX=3 EndY=13 EndZ=0
    g8: LineSegment StartX=27 StartY=13 StartZ=0 EndX=27 EndY=10 EndZ=0
    g9: LineSegment StartX=27 StartY=10 StartZ=0 EndX=37 EndY=10 EndZ=0
    g10: LineSegment StartX=37 StartY=10 StartZ=0 EndX=37 EndY=13 EndZ=0
    g11: LineSegment StartX=37 StartY=13 StartZ=0 EndX=27 EndY=13 EndZ=0
    g12: LineSegment StartX=91 StartY=18 StartZ=0 EndX=94 EndY=18 EndZ=0
    g13: LineSegment StartX=94 StartY=18 StartZ=0 EndX=94 EndY=28 EndZ=0
    g14: LineSegment StartX=94 StartY=28 StartZ=0 EndX=91 EndY=28 EndZ=0
    g15: LineSegment StartX=91 StartY=28 StartZ=0 EndX=91 EndY=18 EndZ=0
    g16: LineSegment [constr] StartX=3 StartY=13 StartZ=0 EndX=91 EndY=28 EndZ=0
  constraints (50):
    c: Coincident(g0,g1)
    c: Coincident(g1,g2)
    c: Coincident(g2,g3)
    c: Coincident(g3,g0)
    c: Vertical(g0)
    c: Vertical(g2)
    c: Horizontal(g1)
    c: Horizontal(g3)
    c: Coincident(g4,g5)
    c: Coincident(g5,g6)
    c: Coincident(g6,g7)
    c: Coincident(g7,g4)
    c: Vertical(g4)
    c: Vertical(g6)
    c: Horizontal(g5)
    c: Horizontal(g7)
    c: Coincident(g4,g0)
    c: Coincident(g8,g9)
    c: Coincident(g9,g10)
    c: Coincident(g10,g11)
    c: Coincident(g11,g8)
    c: Vertical(g8)
    c: Vertical(g10)
    c: Horizontal(g9)
    c: Horizontal(g11)
    c: Coincident(g12,g13)
    c: Coincident(g13,g14)
    c: Coincident(g14,g15)
    c: Coincident(g15,g12)
    c: Horizontal(g12)
    c: Horizontal(g14)
    c: Vertical(g13)
    c: Vertical(g15)
    c: Equal(g0,g7)
    c: Equal(g7,g11)
    c: Equal(g11,g15)
    c: DistanceX(g11,g11) = 10
    c: DistanceX(g1,g1) = 3
    c: Equal(g1,g6)
    c: Equal(g6,g8)
    c: Equal(g8,g12)
    c: Horizontal(g6,g8)
    c: Distance(g1,g-4) = 3
    c: DistanceX(g6,g8) = 14
    c: Distance(g8,g-5) = 3
    c: Distance(g13,g-3) = 3
    c: DistanceY(g10,g14) = 15
    c: Coincident(g16,g0)
    c: Coincident(g16,g14)
    c: Angle(g16,g15) = 1.40196
FEATURE [PartDesign::Pocket] Pocket003
  BaseFeature = -> Pad005
  Direction = (0,1,0)
  Length = 5
  Length2 = 5
  Placement = pos=(0,0,0) rot=(1,0,0;1.5708rad)
  Profile = -> Sketch009
  Refine = true
  Suppressed = false
  Type = 2
FEATURE [PartDesign::LinearPattern] LinearPattern003
  BaseFeature = -> Pocket003
  Direction = -> Sketch009 [V_Axis]
  Length = 160
  Mode = 0
  Occurrences = 3
  Offset = 80
  Originals = -> [Pocket003]
  Placement = pos=(0,0,0) rot=(1,0,0;1.5708rad)
  Refine = true
  Suppressed = false
  TransformMode = 0
FEATURE [Sketcher::SketchObject] Sketch011
  ArcFitTolerance = 0
  ExternalGeometry = -> [LinearPattern003]
  FullyConstrained = true
  MakeInternals = false
  MapMode = 5
  Placement = pos=(0,-3,0) rot=(1,0,0;1.5708rad)
  sketch-geometry (22):
    g0: LineSegment StartX=3 StartY=250 StartZ=0 EndX=3 EndY=247 EndZ=0
    g1: LineSegment StartX=3 StartY=247 StartZ=0 EndX=13 EndY=247 EndZ=0
    g2: LineSegment StartX=13 StartY=247 StartZ=0 EndX=13 EndY=250 EndZ=0
    g3: LineSegment StartX=13 StartY=250 StartZ=0 EndX=3 EndY=250 EndZ=0
    g4: LineSegment StartX=42 StartY=250 StartZ=0 EndX=42 EndY=247 EndZ=0
    g5: LineSegment StartX=42 StartY=247 StartZ=0 EndX=52 EndY=247 EndZ=0
    g6: LineSegment StartX=52 StartY=247 StartZ=0 EndX=52 EndY=250 EndZ=0
    g7: LineSegment StartX=52 StartY=250 StartZ=0 EndX=42 EndY=250 EndZ=0
    g8: LineSegment StartX=81 StartY=247 StartZ=0 EndX=81 EndY=250 EndZ=0
    g9: LineSegment StartX=81 StartY=250 StartZ=0 EndX=91 EndY=250 EndZ=0
    g10: LineSegment StartX=91 StartY=250 StartZ=0 EndX=91 EndY=247 EndZ=0
    g11: LineSegment StartX=91 StartY=247 StartZ=0 EndX=81 EndY=247 EndZ=0
    g12: LineSegment [constr] StartX=13 StartY=250 StartZ=0 EndX=42 EndY=250 EndZ=0
    g13: LineSegment [constr] StartX=52 StartY=250 StartZ=0 EndX=81 EndY=250 EndZ=0
    g14: LineSegment StartX=3 StartY=250 StartZ=0 EndX=3 EndY=260 EndZ=0
    g15: LineSegment StartX=3 StartY=260 StartZ=0 EndX=-1.3e-15 EndY=260 EndZ=0
    g16: LineSegment StartX=-1.3e-15 StartY=260 StartZ=0 EndX=-1.3e-15 EndY=250 EndZ=0
    g17: LineSegment StartX=-1.3e-15 StartY=250 StartZ=0 EndX=3 EndY=250 EndZ=0
    g18: LineSegment StartX=91 StartY=250 StartZ=0 EndX=94 EndY=250 EndZ=0
    g19: LineSegment StartX=94 StartY=250 StartZ=0 EndX=94 EndY=260 EndZ=0
    g20: LineSegment StartX=94 StartY=260 StartZ=0 EndX=91 EndY=260 EndZ=0
    g21: LineSegment StartX=91 StartY=260 StartZ=0 EndX=91 EndY=250 EndZ=0
  constraints (63):
    c: Coincident(g0,g1)
    c: Coincident(g1,g2)
    c: Coincident(g2,g3)
    c: Coincident(g3,g0)
    c: Vertical(g0)
    c: Vertical(g2)
    c: Horizontal(g1)
    c: Horizontal(g3)
    c: Distance(g0,g2) = 10
    c: Distance(g1,g3) = 3
    c: Coincident(g4,g5)
    c: Coincident(g5,g6)
    c: Coincident(g6,g7)
    c: Coincident(g7,g4)
    c: Vertical(g4)
    c: Vertical(g6)
    c: Horizontal(g5)
    c: Horizontal(g7)
    c: Distance(g4,g6) = 10
    c: Distance(g5,g7) = 3
    c: Coincident(g8,g9)
    c: Coincident(g9,g10)
    c: Coincident(g10,g11)
    c: Coincident(g11,g8)
    c: Vertical(g8)
    c: Vertical(g10)
    c: Horizontal(g9)
    c: Horizontal(g11)
    c: Distance(g8,g10) = 10
    c: Distance(g9,g11) = 3
    c: Horizontal(g2,g4)
    c: Distance(g0,g-3) = 6
    c: Distance(g10,g-4) = 6
    c: DistanceY(g-5,g9) = 62
    c: DistanceY(g-6,g-7) = 62
    c: Horizontal(g6,g8)
    c: Coincident(g12,g2)
    c: Coincident(g12,g4)
    c: Coincident(g13,g6)
    c: Coincident(g13,g8)
    c: Equal(g13,g12)
    c: Coincident(g14,g15)
    c: Coincident(g15,g16)
    c: Coincident(g16,g17)
    c: Coincident(g17,g14)
    c: Vertical(g14)
    c: Vertical(g16)
    c: Horizontal(g15)
    c: Horizontal(g17)
    c: Coincident(g14,g0)
    c: DistanceY(g16,g16) = 10
    c: DistanceX(g15,g15) = 3
    c: Coincident(g18,g19)
    c: Coincident(g19,g20)
    c: Coincident(g20,g21)
    c: Coincident(g21,g18)
    c: Horizontal(g18)
    c: Horizontal(g20)
    c: Vertical(g19)
    c: Vertical(g21)
    c: Distance(g19,g21) = 3
    c: Distance(g18,g20) = 10
    c: Coincident(g18,g9)
FEATURE [PartDesign::Pocket] Pocket004
  BaseFeature = -> LinearPattern003
  Direction = (0,1,0)
  Length = 5
  Length2 = 5
  Placement = pos=(0,0,0) rot=(1,0,0;1.5708rad)
  Profile = -> Sketch011
  Refine = true
  Suppressed = false
  Type = 2
FEATURE [Sketcher::SketchObject] Sketch014
  ArcFitTolerance = 0
  AttachmentSupport = -> [Pocket004]
  ExternalGeometry = -> [Pocket004]
  FullyConstrained = true
  MakeInternals = false
  MapMode = 5
  Placement = pos=(0,-3,-3e-15) rot=(1,0,0;1.5708rad)
FEATURE [PartDesign::Body] Body005  label="Side"
  AllowCompound = false
  Group = -> [Sketch008,Pad005,Sketch009,Pocket003,LinearPattern003,Sketch011,Pocket004,Sketch014]
  Origin = -> Origin005
  Placement = pos=(0,0,3) rot=(0,0,1;0rad)
  Tip = -> Pocket004
COMPONENT P10 — same part as P9; its construction recipe is shown at P9.
COMPONENT P11 — recipe-attached ("TopCover001", modeled in this document).
Construction recipe (the document's own serialized feature program — sketch geometry with constraints, then the solid features built on it; lengths are millimeters unless a unit is written):

FEATURE [Sketcher::SketchObject] Sketch010
  ArcFitTolerance = 0
  FullyConstrained = true
  MakeInternals = false
  MapMode = 5
  sketch-geometry (28):
    g0: LineSegment StartX=0 StartY=-3 StartZ=0 EndX=10 EndY=-3 EndZ=0
    g1: LineSegment StartX=10 StartY=-3 StartZ=0 EndX=10 EndY=0 EndZ=0
    g2: LineSegment StartX=49 StartY=0 StartZ=0 EndX=78 EndY=0 EndZ=0
    g3: LineSegment StartX=78 StartY=0 StartZ=0 EndX=78 EndY=-3 EndZ=0
    g4: LineSegment StartX=78 StartY=-3 StartZ=0 EndX=88 EndY=-3 EndZ=0
    g5: LineSegment StartX=88 StartY=-3 StartZ=0 EndX=88 EndY=12 EndZ=0
    g6: LineSegment StartX=91 StartY=12 StartZ=0 EndX=91 EndY=382 EndZ=0
    g7: LineSegment StartX=91 StartY=382 StartZ=0 EndX=88 EndY=382 EndZ=0
    g8: LineSegment StartX=88 StartY=382 StartZ=0 EndX=88 EndY=397 EndZ=0
    g9: LineSegment StartX=88 StartY=397 StartZ=0 EndX=78 EndY=397 EndZ=0
    g10: LineSegment StartX=78 StartY=397 StartZ=0 EndX=78 EndY=394 EndZ=0
    g11: LineSegment StartX=78 StartY=394 StartZ=0 EndX=49 EndY=394 EndZ=0
    g12: LineSegment StartX=10 StartY=394 StartZ=0 EndX=10 EndY=397 EndZ=0
    g13: LineSegment StartX=10 StartY=397 StartZ=0 EndX=0 EndY=397 EndZ=0
    g14: LineSegment StartX=0 StartY=397 StartZ=0 EndX=0 EndY=382 EndZ=0
    g15: LineSegment StartX=0 StartY=382 StartZ=0 EndX=-3 EndY=382 EndZ=0
    g16: LineSegment StartX=-3 StartY=12 StartZ=0 EndX=-3 EndY=382 EndZ=0
    g17: LineSegment StartX=39 StartY=394 StartZ=0 EndX=39 EndY=397 EndZ=0
    g18: LineSegment StartX=39 StartY=397 StartZ=0 EndX=49 EndY=397 EndZ=0
    g19: LineSegment StartX=49 StartY=397 StartZ=0 EndX=49 EndY=394 EndZ=0
    g20: LineSegment StartX=39 StartY=394 StartZ=0 EndX=10 EndY=394 EndZ=0
    g21: LineSegment StartX=39 StartY=0 StartZ=0 EndX=39 EndY=-3 EndZ=0
    g22: LineSegment StartX=39 StartY=-3 StartZ=0 EndX=49 EndY=-3 EndZ=0
    g23: LineSegment StartX=49 StartY=-3 StartZ=0 EndX=49 EndY=0 EndZ=0
    g24: LineSegment StartX=10 StartY=0 StartZ=0 EndX=39 EndY=0 EndZ=0
    g25: LineSegment StartX=-3 StartY=12 StartZ=0 EndX=0 EndY=12 EndZ=0
    g26: LineSegment StartX=0 StartY=12 StartZ=0 EndX=0 EndY=-3 EndZ=0
    g27: LineSegment StartX=88 StartY=12 StartZ=0 EndX=91 EndY=12 EndZ=0
  constraints (88):
    c: Horizontal(g0)
    c: Coincident(g0,g1)
    c: PointOnObject(g1,g-1)
    c: Vertical(g1)
    c: PointOnObject(g2,g-1)
    c: Coincident(g2,g3)
    c: Vertical(g3)
    c: Coincident(g3,g4)
    c: Horizontal(g4)
    c: Coincident(g4,g5)
    c: Vertical(g6)
    c: Coincident(g6,g7)
    c: Horizontal(g7)
    c: Coincident(g7,g8)
    c: Coincident(g8,g9)
    c: Horizontal(g9)
    c: Coincident(g9,g10)
    c: Vertical(g10)
    c: Coincident(g10,g11)
    c: Horizontal(g11)
    c: Coincident(g20,g12)
    c: Vertical(g12)
    c: Coincident(g12,g13)
    c: Horizontal(g13)
    c: Coincident(g13,g14)
    c: Vertical(g14)
    c: Coincident(g14,g15)
    c: Horizontal(g15)
    c: Vertical(g8)
    c: Vertical(g5)
    c: Coincident(g16,g15)
    c: Vertical(g16)
    c: Equal(g12,g10)
    c: Equal(g10,g1)
    c: Equal(g1,g3)
    c: DistanceX(g0,g0) = 10
    c: Equal(g0,g4)
    c: Equal(g4,g13)
    c: Equal(g13,g9)
    c: Equal(g14,g8)
    c: DistanceY(g0,g13) = 400
    c: DistanceX(g15,g6) = 94
    c: PointOnObject(g14,g-2)
    c: Equal(g15,g7)
    c: DistanceX(g16,g-1) = 3
    c: PointOnObject(g17,g20)
    c: Vertical(g17)
    c: Coincident(g17,g18)
    c: Horizontal(g18)
    c: Coincident(g18,g19)
    c: Vertical(g19)
    c: Coincident(g11,g19)
    c: PointOnObject(g20,g17)
    c: Equal(g12,g17)
    c: Horizontal(g20)
    c: Equal(g13,g18)
    c: Equal(g19,g17)
    c: Equal(g20,g11)
    c: DistanceX(g12,g17) = 29
    c: Coincident(g21,g22)
    c: Coincident(g22,g23)
    c: Vertical(g21)
    c: Vertical(g23)
    c: Horizontal(g22)
    c: Equal(g23,g3)
    c: Equal(g22,g4)
    c: Coincident(g24,g1)
    c: Coincident(g24,g21)
    c: Horizontal(g24)
    c: Coincident(g23,g2)
    c: Horizontal(g2)
    c: Equal(g24,g2)
    c: DistanceX(g2,g2) = 29
    c: DistanceX(g24,g24) = 29
    c: Coincident(g25,g16)
    c: PointOnObject(g25,g-2)
    c: Horizontal(g25)
    c: Coincident(g26,g25)
    c: Coincident(g26,g0)
    c: Vertical(g26)
    c: DistanceY(g26,g26) = 15
    c: Distance(g1,g1) = 3
    c: Coincident(g27,g5)
    c: Coincident(g27,g6)
    c: Horizontal(g27)
    c: Horizontal(g25,g5)
    c: Equal(g27,g25)
    c: DistanceY(g14,g14) = 15
FEATURE [PartDesign::Pad] Pad006
  Direction = (0,0,1)
  Length = 3
  Length2 = 10
  Profile = -> Sketch010
  Refine = true
  Suppressed = false
  Type = 0
FEATURE [Sketcher::SketchObject] Sketch012
  ArcFitTolerance = 0
  ExternalGeometry = -> [Pad006]
  FullyConstrained = false
  MakeInternals = false
  MapMode = 5
  Placement = pos=(0,0,3) rot=(0,0,1;0rad)
  sketch-geometry (8):
    g0: LineSegment StartX=0 StartY=22 StartZ=0 EndX=-3 EndY=22 EndZ=0
    g1: LineSegment StartX=-3 StartY=22 StartZ=0 EndX=-3 EndY=32 EndZ=0
    g2: LineSegment StartX=-3 StartY=32 StartZ=0 EndX=0 EndY=32 EndZ=0
    g3: LineSegment StartX=0 StartY=32 StartZ=0 EndX=0 EndY=22 EndZ=0
    g4: LineSegment StartX=91 StartY=22 StartZ=0 EndX=91 EndY=32 EndZ=0
    g5: LineSegment StartX=91 StartY=32 StartZ=0 EndX=88 EndY=32 EndZ=0
    g6: LineSegment StartX=88 StartY=32 StartZ=0 EndX=88 EndY=22 EndZ=0
    g7: LineSegment StartX=88 StartY=22 StartZ=0 EndX=91 EndY=22 EndZ=0
  constraints (24):
    c: Coincident(g0,g1)
    c: Coincident(g1,g2)
    c: Coincident(g2,g3)
    c: Coincident(g3,g0)
    c: Horizontal(g0)
    c: Horizontal(g2)
    c: Vertical(g1)
    c: Vertical(g3)
    c: Distance(g1,g3) = 3
    c: Distance(g0,g2) = 10
    c: DistanceY(g-4,g0) = 10
    c: Coincident(g4,g5)
    c: Coincident(g5,g6)
    c: Coincident(g6,g7)
    c: Coincident(g7,g4)
    c: Vertical(g4)
    c: Vertical(g6)
    c: Horizontal(g5)
    c: Horizontal(g7)
    c: Distance(g4,g6) = 3
    c: Distance(g5,g7) = 10
    c: PointOnObject(g4,g-5)
    c: DistanceY(g-5,g4) = 10
    c: PointOnObject(g0,g-4)
FEATURE [PartDesign::Pocket] Pocket005
  BaseFeature = -> Pad006
  Direction = (0,0,-1)
  Length = 5
  Length2 = 5
  Profile = -> Sketch012
  Refine = true
  Suppressed = false
  Type = 2
FEATURE [PartDesign::LinearPattern] LinearPattern004
  BaseFeature = -> Pocket005
  Direction = -> Sketch012 [V_Axis]
  Length = 340
  Mode = 0
  Occurrences = 3
  Offset = 170
  Originals = -> [Pocket005]
  Refine = true
  Suppressed = false
  TransformMode = 0
FEATURE [PartDesign::Body] Body006  label="TopCover"
  AllowCompound = false
  Group = -> [Sketch010,Pad006,Sketch012,Pocket005,LinearPattern004]
  Origin = -> Origin009
  Placement = pos=(3,0,13) rot=(0,0,1;0rad)
  Tip = -> LinearPattern004
PROVENANCE & LICENSES
A FreeCAD (.FCStd) document from a public repository crawl; recipes are the document's own serialized feature recipes (and, for linked parts, companion documents' recipes).
License: mit.
